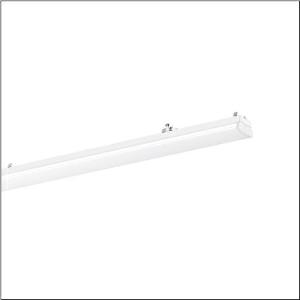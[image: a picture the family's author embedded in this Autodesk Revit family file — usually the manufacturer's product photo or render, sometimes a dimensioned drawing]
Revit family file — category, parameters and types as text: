
# Revit family: licross_r__11_recessed_opal_mo_51tl1ddv495g_cbeb
name_source: partatom
category: Lighting Fixtures
units: mm (PartAtom-declared; Revit-internal decimal feet)

## family parameters
Cut with Voids When Loaded = No
Host = Face
Light Source = No
Part Type = Normal
Room Calculation Point = No
Round Connector Dimension = Use Diameter
Shared = No

## types (1)
- --- (1 x LED, 9500 lm, 52.6 W, 4000K)
    Apparent Load = 53 VA
    CIE Flux Codes = 44 73 91 87 100
    Color Rendering = 80
    Color Temperature = 4000K
    Default Elevation = 1800 mm
    Description = Licross® 11 recessed opal MO, luminaire insert, of sheet steel, coil coated, white, length: 2.250mm, width: 76mm, height: 87mm, LED rated luminous flux: 9.500lm, light colour: 840, control gear: DALI 2, with plug, 5-pole, with phase selection, mains connection: 220..240V, AC, 50/60Hz, rated input power: 53W, halogen-free wiring, primary optical cover: cover, of PMMA, light emission: direct with ceiling illumination distribution, primary light characteristic: symmetric, protection rating (complete): IP40, insulation class (complete): insulation class I (protective earthing), certification: CE, ENEC, VDE, UKCA, protection symbol: D if used in an environment without relevant dust loads with corresponding accessories, impact resistance: IK06, permissible ambient temperature for indoor applications: -25..+40°C, corresponds to IFS (International Featured Standards) requirements for safety and quality in the food industry, reducing of maximum allowable ambient temperature of 5°C with ceiling mounting, LABS conformity tested according to VDMA 24364:2018-05, packaging unit: 1 piece
    Height = 83 mm
    Lamp = 1 x LED
    Lamp Light Flux = 9500 lm
    Lamp Power = 52.6 W
    Lamp count = 1
    Length = 2250 mm
    Luminous efficacy = 181 lm/W
    Manufacturer = Siteco
    ModVariant = No
    Model = 51TL1DDV495G
    Mounting Place = Ceiling
    Mounting Type = Pendant
    Number of Poles = 1
    OnlyDefault = Yes
    Power Factor = 1
    Product Name = Licross® 11 recessed opal MO
    Product group = luminaire insert
    ProductGroupID = 901
    Protection Class = Protection class I
    Protection Degree = IP 40
    RLX_Detail_Level = 1
    RLX_Emergency_Light_Flux = 0 lm
    RLX_Emergency_Type = 0
    RLX_Emergency_Type_DB = No
    RlxData = <blob elided: 17989 chars, md5=acddf0de>
    Socket = socket
    Standby Power = 0 W
    System Light Flux = 9500 lm
    System Power = 53 W
    Type Comments = factory setting: luminous flux: 100 % | dim-lin: 254 | 239 mA
    Type Image = l_1313666.jpg
    URL = http://relux.com
    VarID = @adj_027629
    Voltage = 0 V
    Weight = 0.00 kg
    Width = 76 mm

## geometry (parser evidence)
native form markers: Blend x4, Sweep x12
no freeform markers — native parametric forms only
